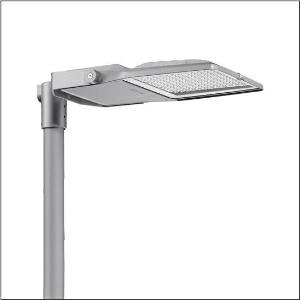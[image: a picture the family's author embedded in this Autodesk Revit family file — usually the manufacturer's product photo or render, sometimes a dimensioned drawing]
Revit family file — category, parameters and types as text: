
# Revit family: floodlight_fl_21_midi___pl61_5xa7785f2c3a_30c2
name_source: partatom
category: Lighting Fixtures
units: mm (PartAtom-declared; Revit-internal decimal feet)

## family parameters
Cut with Voids When Loaded = No
Host = Face
Light Source = No
Part Type = Normal
Room Calculation Point = No
Round Connector Dimension = Use Diameter
Shared = No

## types (1)
- --- (1 x LED, 35100 lm, 271.6 W, 3000K)
    Apparent Load = 272 VA
    CIE Flux Codes = 33 65 98 100 100
    Color Rendering = 70
    Color Temperature = 3000K
    Default Elevation = 1800 mm
    Description = Floodlight FL 21 midi, floodlight, primary light control with lens, of PMMA, primary optical cover: protective disc, of toughened safety glass, transparent, light distribution: PL61, light emission: direct distribution, installation type: surface-mounted, LED, High Power LED, rated luminous flux: 35.100lm, luminous efficacy: 129lm/W, light colour: 730, colour temperature: 3000K, control gear: ECG Smart Interface, control: flexible luminous flux parameterisation, time-dependent luminous flux control, constant luminous flux control, overheat protection, presetting dimming logarithmic, with terminal, 6-pole, mains connection: 220..240V, AC, 50/60Hz, start of lifetime: 272W, end of service life: 287W, reduction: 123W, luminaire housing, of diecast aluminium, powder-coated, Siteco® metallic grey (DB 702S), sealing non-destructively replaceable, please order mast flange separately, mast bracket, of steel, galvanised, powder-coated, Siteco® metallic grey (DB 702S), Smart Interface above, protection rating (complete): IP66, insulation class (complete): insulation class II (safety insulation), certification: CE, protection symbol: D, impact resistance: IK08, permissible operating ambient temperature: -40..+40°C, permissible operating ambient temperature for outdoor applications: -40..+50°C, standard: DIN EN 12944, LABS conformity tested according to VDMA 24364:2018-05, packaging unit: 1 piece

Light Distribution: PL61
    Height = 76 mm
    Lamp = 1 x LED
    Lamp Light Flux = 35100 lm
    Lamp Power = 271.6 W
    Lamp count = 1
    Length = 657 mm
    Luminous efficacy = 129 lm/W
    Manufacturer = Siteco
    ModVariant = No
    Model = 5XA7785F2C3A
    Number of Poles = 1
    OnlyDefault = Yes
    Power Factor = 1
    Product Name = Floodlight FL 21 midi | PL61
    Product group = floodlight | pylon annexe
    ProductGroupID = 6200
    Protection Class = Protection class II
    Protection Degree = IP 66
    RLX_Detail_Level = 1
    RLX_Emergency_Light_Flux = 0 lm
    RLX_Emergency_Type = 0
    RLX_Emergency_Type_DB = No
    RlxData = <blob elided: 153481 chars, md5=3bd8c3d1>
    Socket = socket
    Standby Power = 0 W
    System Light Flux = 35100 lm
    System Power = 272 W
    Type Comments = factory setting: luminous flux: 100 % | dim-lin: 254 | 620 mA
    Type Image = l_1007123.jpg
    URL = http://relux.com
    VarID = @adj_146645
    Voltage = 0 V
    Weight = 0.00 kg
    Width = 442 mm

## geometry (parser evidence)
native form markers: Blend x4, Sweep x15
no freeform markers — native parametric forms only
